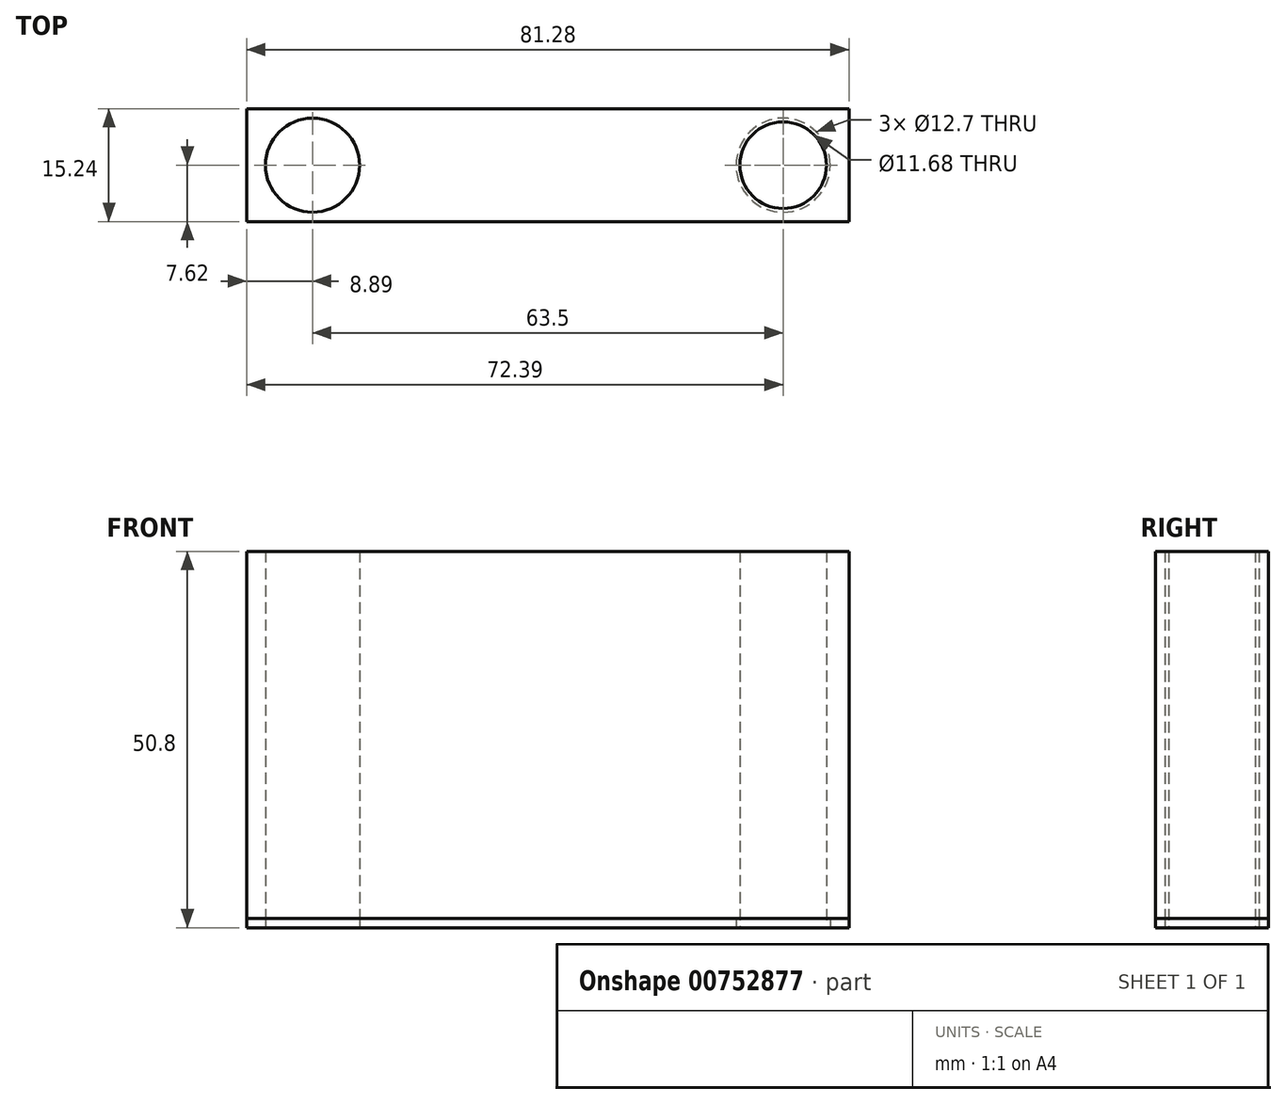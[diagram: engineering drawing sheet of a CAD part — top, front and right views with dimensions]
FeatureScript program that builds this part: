
annotation { "Feature Type Name" : "Feature", "Feature Type Description" : "" }
export const myFeature = defineFeature(function(context is Context, id is Id, definition is map)
    precondition{}
    {
        {
            var Q0;
            Q0=qCreatedBy(makeId("Top.planeOp"),FACE);
            var sketch = newSketch(context, id + "F0", { "sketchPlane" : qUnion([Q0])});
            skLineSegment(sketch, "E0.bottom", {"start": v(40.64, 7.62) * mm, "end": v(-40.64, 7.62) * mm});
            skLineSegment(sketch, "E0.top", {"start": v(40.64, -7.62) * mm, "end": v(-40.64, -7.62) * mm});
            skLineSegment(sketch, "E0.left", {"start": v(40.64, 7.62) * mm, "end": v(40.64, -7.62) * mm});
            skLineSegment(sketch, "E0.right", {"start": v(-40.64, 7.62) * mm, "end": v(-40.64, -7.62) * mm});
            skPoint(sketch, "E0.middle", {"position": v(0, 0) * mm});
            skCircle(sketch, "E1", {"center": v(31.75, 0) * mm, "radius": 6.35 * mm});
            skCircle(sketch, "E2.MirrorC", {"center": v(-31.75, 0) * mm, "radius": 6.35 * mm});
            skCircle(sketch, "E3", {"center": v(31.75, 0) * mm, "radius": 5.84 * mm});
            skCircle(sketch, "E4.MirrorC", {"center": v(-31.75, 0) * mm, "radius": 5.84 * mm});
            skSolve(sketch);
        }
        {
            var Q0;
            Q0=makeQuery(id+"F0.imprint","IMPRINT",FACE,{"disambiguationData":[TD([[makeQuery(id+"F0.imprint","IMPRINT",EDGE,{"derivedFrom":sQuery(id+"F0.wireOp",EDGE,"E2.MirrorC")}),-1.0]])]});
            var Q1;
            Q1=makeQuery(id+"F0.imprint","IMPRINT",FACE,{"disambiguationData":[TD([[makeQuery(id+"F0.imprint","IMPRINT",EDGE,{"derivedFrom":sQuery(id+"F0.wireOp",EDGE,"E1")}),1.0]])]});
            extrude(context, id + "F1", {"entities" : qUnion([Q0, Q1]), "depth" : 50.8 * mm, "offsetDistance" : 25.4 * mm});
        }
        {
            var Q0;
            Q0=makeQuery(id+"F0.imprint","IMPRINT",FACE,{"disambiguationData":[TD([[makeQuery(id+"F0.imprint","IMPRINT",EDGE,{"derivedFrom":sQuery(id+"F0.wireOp",EDGE,"E0.bottom")}),1.0]])]});
            extrude(context, id + "F2", {"entities" : qUnion([Q0]), "depth" : 1.27 * mm, "offsetDistance" : 25.4 * mm});
        }
    });
